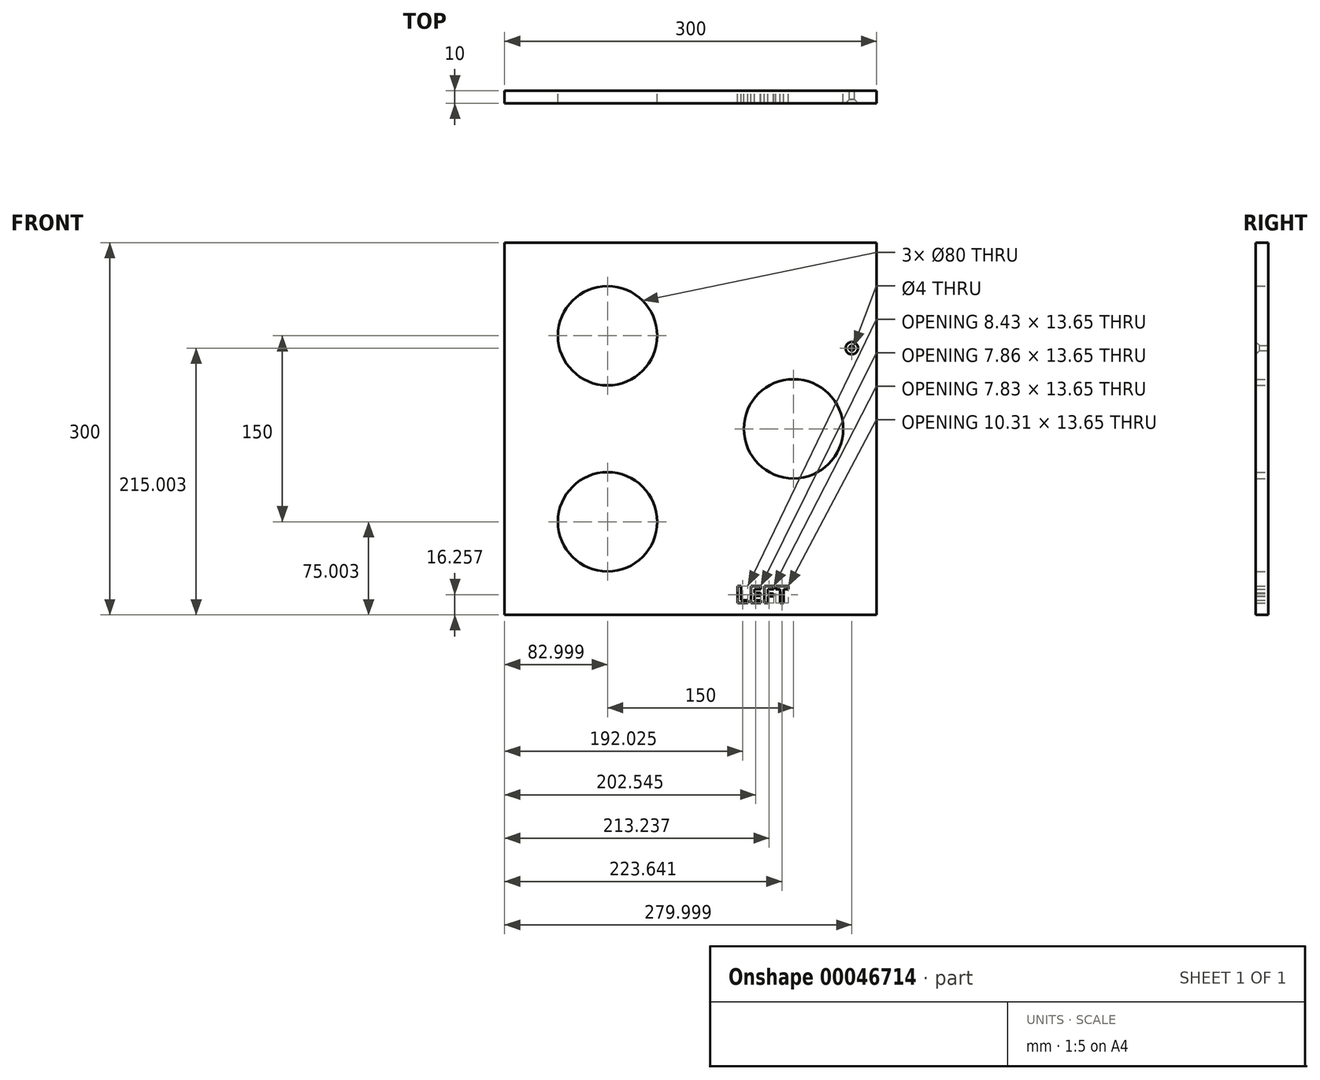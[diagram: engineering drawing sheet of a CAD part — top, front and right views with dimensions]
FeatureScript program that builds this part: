
annotation { "Feature Type Name" : "Feature", "Feature Type Description" : "" }
export const myFeature = defineFeature(function(context is Context, id is Id, definition is map)
    precondition{}
    {
        {
            var Q0;
            Q0=qCreatedBy(makeId("Front.planeOp"),FACE);
            var sketch = newSketch(context, id + "F0", { "sketchPlane" : qUnion([Q0])});
            skLineSegment(sketch, "E0.bottom", {"start": v(-151.27, 151.55) * mm, "end": v(148.73, 151.55) * mm});
            skLineSegment(sketch, "E0.top", {"start": v(-151.27, -148.45) * mm, "end": v(148.73, -148.45) * mm});
            skLineSegment(sketch, "E0.left", {"start": v(-151.27, 151.55) * mm, "end": v(-151.27, -148.45) * mm});
            skLineSegment(sketch, "E0.right", {"start": v(148.73, 151.55) * mm, "end": v(148.73, -148.45) * mm});
            skCircle(sketch, "E1", {"center": v(-68.27, 76.55) * mm, "radius": 40 * mm});
            skCircle(sketch, "E2", {"center": v(81.73, 1.55) * mm, "radius": 40 * mm});
            skCircle(sketch, "E3", {"center": v(-68.27, -73.45) * mm, "radius": 40 * mm});
            skLineSegment(sketch, "E4", {"start": v(14.73, 177.05) * mm, "end": v(14.73, -173.66) * mm, "construction": true});
            skCircle(sketch, "E5", {"center": v(128.73, 66.55) * mm, "radius": 2 * mm});
            skText(sketch, "E6", { "text": "LEFT", "fontName": "OpenSans-Bold.ttf"});
            const initialGuessF0  = {"E6": [0.03482, -0.13902, 1, 0, 0.01377]};
            skSetInitialGuess(sketch, initialGuessF0);
            skSolve(sketch);
        }
        {
            var Q0;
            Q0=makeQuery(id+"F0.imprint","IMPRINT",FACE,{"disambiguationData":[TD([[makeQuery(id+"F0.imprint","IMPRINT",EDGE,{"derivedFrom":sQuery(id+"F0.wireOp",EDGE,"E0.bottom")}),-1.0]])]});
            extrude(context, id + "F1", {"entities" : qUnion([Q0]), "depth" : 10 * mm});
        }
        {
            var Q0;
            Q0=makeQuery(id+"F1.opExtrude","CAP_EDGE",EDGE,{"disambiguationData":[OSD([sQuery(id+"F0.wireOp",EDGE,"E5")])],"isStart":false});
            chamfer(context, id + "F2", {"entities" : qUnion([Q0]), "width" : 3 * mm, "tangentPropagation" : true});
        }
    });
